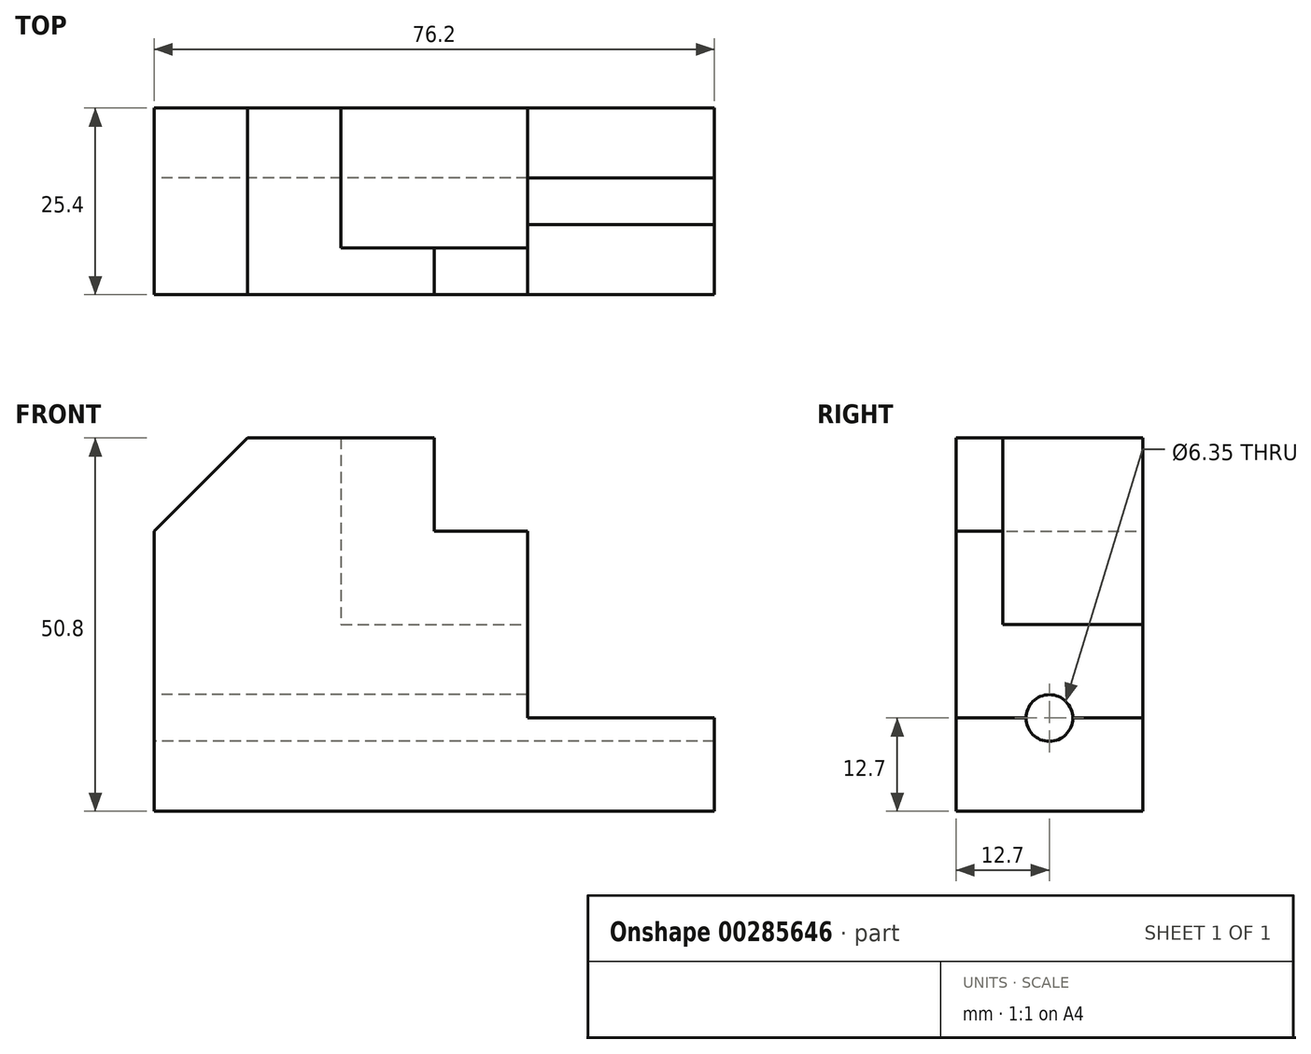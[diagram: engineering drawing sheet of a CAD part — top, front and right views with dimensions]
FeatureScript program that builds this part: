
annotation { "Feature Type Name" : "Feature", "Feature Type Description" : "" }
export const myFeature = defineFeature(function(context is Context, id is Id, definition is map)
    precondition{}
    {
        {
            var Q0;
            Q0=qCreatedBy(makeId("Front.planeOp"),FACE);
            var sketch = newSketch(context, id + "F0", { "sketchPlane" : qUnion([Q0])});
            skLineSegment(sketch, "E0", {"start": v(0, 0) * mm, "end": v(76.2, 0) * mm});
            skLineSegment(sketch, "E1", {"start": v(76.2, 0) * mm, "end": v(76.2, 12.7) * mm});
            skLineSegment(sketch, "E2", {"start": v(76.2, 12.7) * mm, "end": v(50.8, 12.7) * mm});
            skLineSegment(sketch, "E3", {"start": v(50.8, 12.7) * mm, "end": v(50.8, 38.1) * mm});
            skLineSegment(sketch, "E4", {"start": v(50.8, 38.1) * mm, "end": v(38.1, 38.1) * mm});
            skLineSegment(sketch, "E5", {"start": v(38.1, 38.1) * mm, "end": v(38.1, 50.8) * mm});
            skLineSegment(sketch, "E6", {"start": v(38.1, 50.8) * mm, "end": v(12.7, 50.8) * mm});
            skLineSegment(sketch, "E7", {"start": v(12.7, 50.8) * mm, "end": v(0, 38.1) * mm});
            skLineSegment(sketch, "E8", {"start": v(0, 38.1) * mm, "end": v(0, 0) * mm});
            skSolve(sketch);
        }
        {
            var Q0;
            Q0 = qSketchRegion(id + "F0", true);
            extrude(context, id + "F1", {"entities" : qUnion([Q0]), "endBound" : BoundingType.SYMMETRIC, "depth" : 25.4 * mm});
        }
        {
            var Q0;
            Q0=qCreatedBy(makeId("Front.planeOp"),FACE);
            var sketch = newSketch(context, id + "F2", { "sketchPlane" : qUnion([Q0])});
            skLineSegment(sketch, "E9", {"start": v(25.4, 50.8) * mm, "end": v(25.4, 25.4) * mm});
            skLineSegment(sketch, "E10", {"start": v(25.4, 25.4) * mm, "end": v(50.8, 25.4) * mm});
            skLineSegment(sketch, "E11", {"start": v(25.4, 50.8) * mm, "end": v(38.1, 50.8) * mm});
            skPoint(sketch, "E11.endSnap0", {"position": v(38.1, 25.4) * mm});
            skLineSegment(sketch, "E12", {"start": v(38.1, 50.8) * mm, "end": v(38.1, 38.1) * mm});
            skLineSegment(sketch, "E13", {"start": v(38.1, 38.1) * mm, "end": v(50.8, 38.1) * mm});
            skLineSegment(sketch, "E14", {"start": v(50.8, 38.1) * mm, "end": v(50.8, 25.4) * mm});
            skSolve(sketch);
        }
        {
            var Q0;
            Q0 = qSketchRegion(id + "F2", true);
            extrude(context, id + "F3", {"entities" : qUnion([Q0]), "operationType" : NewBodyOperationType.REMOVE, "oppositeDirection" : true, "depth" : 25.4 * mm});
        }
        {
            var Q0;
            Q0 = qSketchRegion(id + "F2", true);
            extrude(context, id + "F4", {"entities" : qUnion([Q0]), "operationType" : NewBodyOperationType.REMOVE, "endBound" : BoundingType.SYMMETRIC, "oppositeDirection" : true, "depth" : 12.7 * mm});
        }
        {
            var Q0;
            Q0=qCreatedBy(makeId("Right.planeOp"),FACE);
            var sketch = newSketch(context, id + "F5", { "sketchPlane" : qUnion([Q0])});
            skCircle(sketch, "E15", {"center": v(0, 12.7) * mm, "radius": 3.18 * mm});
            skSolve(sketch);
        }
        {
            var Q0;
            Q0 = qSketchRegion(id + "F5", true);
            extrude(context, id + "F6", {"entities" : qUnion([Q0]), "operationType" : NewBodyOperationType.REMOVE, "endBound" : BoundingType.THROUGH_ALL, "depth" : 25.4 * mm});
        }
    });
